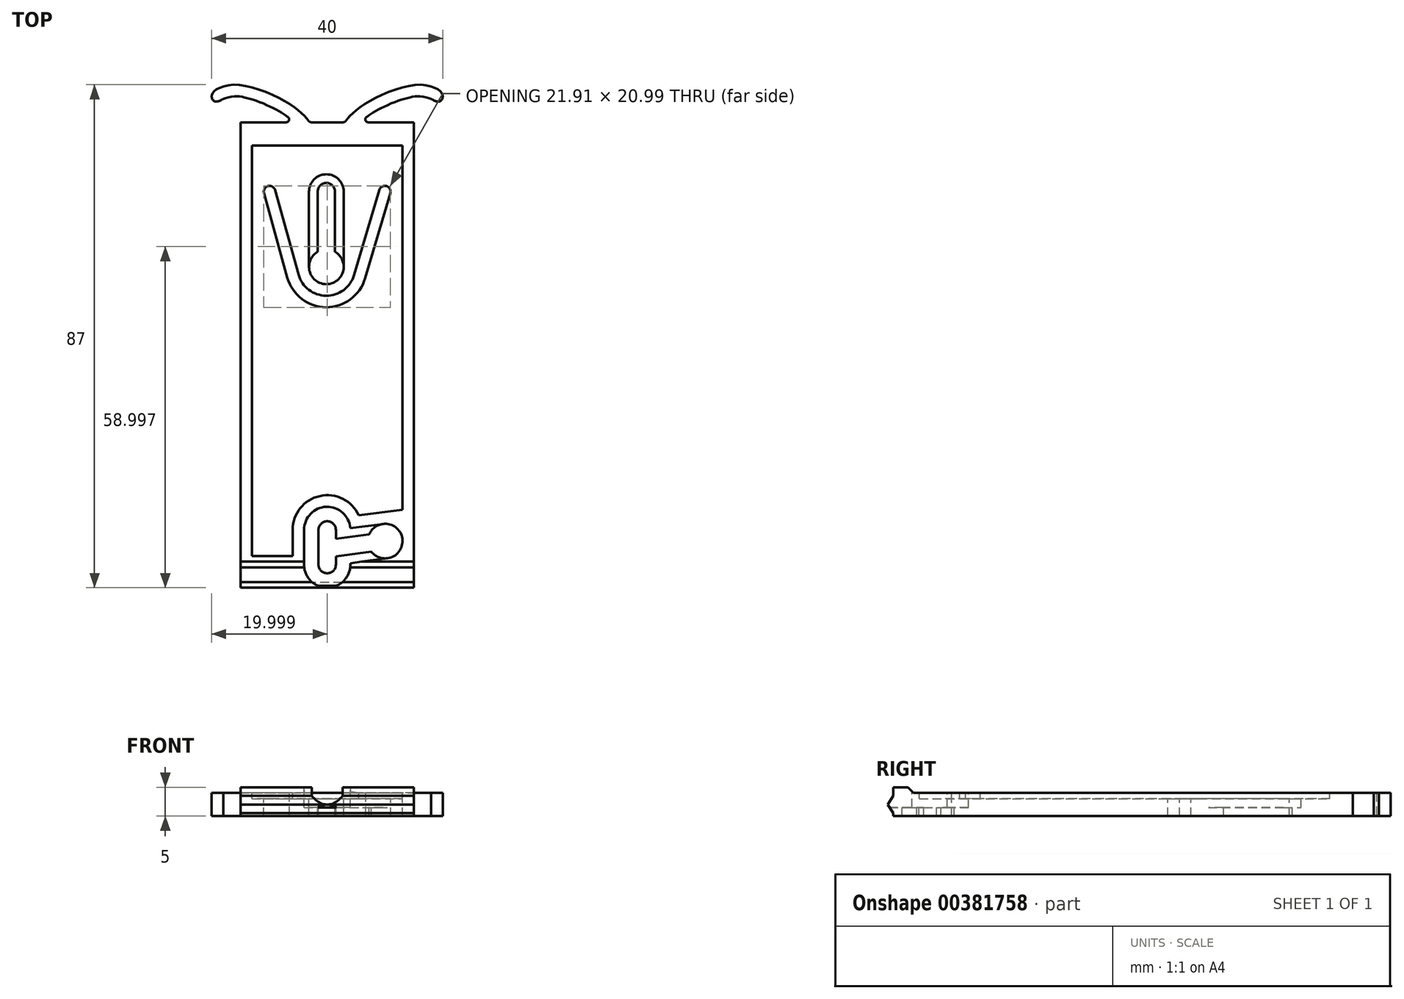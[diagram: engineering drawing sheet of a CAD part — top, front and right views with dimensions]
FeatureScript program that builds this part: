
annotation { "Feature Type Name" : "Feature", "Feature Type Description" : "" }
export const myFeature = defineFeature(function(context is Context, id is Id, definition is map)
    precondition{}
    {
        {
            var Q0;
            Q0=qCreatedBy(makeId("Top.planeOp"),FACE);
            var sketch = newSketch(context, id + "F0", { "sketchPlane" : qUnion([Q0])});
            skLineSegment(sketch, "E0.right", {"start": v(30.36, 0) * mm, "end": v(30.36, -80.5) * mm});
            skLineSegment(sketch, "E1", {"start": v(15.36, -84.44) * mm, "end": v(15.36, 27.39) * mm, "construction": true});
            skPoint(sketch, "E1.endSnap0", {"position": v(15.36, 0) * mm});
            skLineSegment(sketch, "E2", {"start": v(-4.64, 6.5) * mm, "end": v(31.36, 6.5) * mm, "construction": true});
            skLineSegment(sketch, "E3.MirrorCS", {"start": v(18.36, 6.5) * mm, "end": v(18.36, 0) * mm, "construction": true});
            skLineSegment(sketch, "E4.0", {"start": v(-5, 5.5) * mm, "end": v(35.36, 5.5) * mm, "construction": true});
            skLineSegment(sketch, "E5", {"start": v(31.36, 9.18) * mm, "end": v(31.36, -0.18) * mm, "construction": true});
            skLineSegment(sketch, "E6", {"start": v(14.49, 3) * mm, "end": v(22.26, 3) * mm, "construction": true});
            skLineSegment(sketch, "E7", {"start": v(21.36, 4) * mm, "end": v(21.36, 1.65) * mm, "construction": true});
            skLineSegment(sketch, "E8.trimOffspring", {"start": v(22.44, 0) * mm, "end": v(30.36, 0) * mm});
            skPoint(sketch, "E9.visualSharp", {"position": v(18.36, 0) * mm});
            skLineSegment(sketch, "E10", {"start": v(35.36, 5.5) * mm, "end": v(35.36, 4.5) * mm});
            skLineSegment(sketch, "E11.trimOffspring", {"start": v(31.82, 6.5) * mm, "end": v(35.36, 6.5) * mm, "construction": true});
            skFitSpline(sketch, "E12", {"points": [v(35.36, 4.5) * mm, v(35.09, 5.18) * mm, v(31.36, 6.5) * mm, v(21.36, 2.82) * mm, v(18.36, 0) * mm], "startDerivative": vector(-1.02, 6.23) * mm, "endDerivative": vector(-8.9, -10.77) * mm});
            skFitSpline(sketch, "E13.0", {"points": [v(34.37, 4.34) * mm, v(34.36, 4.4) * mm, v(34.35, 4.5) * mm, v(34.34, 4.51) * mm, v(34.34, 4.52) * mm, v(34.31, 4.55) * mm, v(34.25, 4.62) * mm, v(34.1, 4.74) * mm, v(33.84, 4.91) * mm, v(33.5, 5.09) * mm, v(32.95, 5.3) * mm, v(32.27, 5.45) * mm, v(31.49, 5.5) * mm, v(30.63, 5.48) * mm, v(29.4, 5.3) * mm, v(27.26, 4.7) * mm, v(24.5, 3.55) * mm, v(21.73, 1.95) * mm, v(20.2, 0.64) * mm, v(19.5, -0.19) * mm, v(19.13, -0.64) * mm], "construction": true});
            skPoint(sketch, "E14.third.point", {"position": v(33.58, 3.88) * mm});
            skPoint(sketch, "E15", {"position": v(31.36, 4.5) * mm});
            skPoint(sketch, "E16", {"position": v(27.51, 3.67) * mm});
            skPoint(sketch, "E17", {"position": v(24.47, 2.34) * mm});
            skPoint(sketch, "E18", {"position": v(21.04, 0) * mm});
            skPoint(sketch, "E19", {"position": v(22.66, 1.29) * mm});
            skPoint(sketch, "E20", {"position": v(29.8, 4.32) * mm});
            skFitSpline(sketch, "E21", {"points": [v(33.58, 3.88) * mm, v(33.32, 4.05) * mm, v(31.36, 4.5) * mm, v(29.8, 4.32) * mm, v(27.51, 3.67) * mm, v(24.47, 2.34) * mm, v(22.66, 1.29) * mm, v(21.04, 0) * mm], "startDerivative": vector(-2.9, 2.85) * mm, "endDerivative": vector(-10.67, -8.94) * mm});
            skPoint(sketch, "E22", {"position": v(33.84, 3.77) * mm});
            skPoint(sketch, "E23", {"position": v(34.3, 3.61) * mm});
            skPoint(sketch, "E24", {"position": v(34.8, 3.6) * mm});
            skPoint(sketch, "E25", {"position": v(35.23, 4) * mm});
            skFitSpline(sketch, "E26", {"points": [v(33.32, 4.05) * mm, v(33.84, 3.77) * mm, v(34.3, 3.61) * mm, v(34.8, 3.6) * mm, v(35.23, 4) * mm, v(35.36, 4.5) * mm], "startDerivative": vector(2.5, -1.5) * mm, "endDerivative": vector(0.35, 2.57) * mm});
            skLineSegment(sketch, "E27", {"start": v(18.13, 0) * mm, "end": v(15.36, 0) * mm});
            skLineSegment(sketch, "E28", {"start": v(30.36, -80.5) * mm, "end": v(15.36, -80.5) * mm});
            skArc(sketch, "E29.filletArc", {"start": v(18.13, 0) * mm, "mid": v(18.34, 0.05) * mm, "end": v(18.51, 0.18) * mm});
            skArc(sketch, "E30.filletArc", {"start": v(22.14, 0.9) * mm, "mid": v(21.97, 0.34) * mm, "end": v(22.44, 0) * mm});
            skLineSegment(sketch, "E31.MirrorCS", {"start": v(0.36, 0) * mm, "end": v(0.36, -80.5) * mm});
            skFitSpline(sketch, "E32.MirrorCS", {"points": [v(-2.86, 3.88) * mm, v(-2.6, 4.05) * mm, v(-0.64, 4.5) * mm, v(0.92, 4.32) * mm, v(3.21, 3.67) * mm, v(6.25, 2.34) * mm, v(8.06, 1.29) * mm, v(9.68, 0) * mm], "startDerivative": vector(2.9, 2.85) * mm, "endDerivative": vector(10.67, -8.94) * mm});
            skFitSpline(sketch, "E33.MirrorCS", {"points": [v(-2.86, 3.88) * mm, v(-2.6, 4.05) * mm, v(-0.64, 4.5) * mm, v(0.92, 4.32) * mm, v(3.21, 3.67) * mm, v(6.25, 2.34) * mm, v(8.06, 1.29) * mm, v(9.68, 0) * mm], "startDerivative": vector(2.9, 2.85) * mm, "endDerivative": vector(10.67, -8.94) * mm});
            skArc(sketch, "E34.MirrorCS", {"start": v(8.59, 0.9) * mm, "mid": v(8.75, 0.34) * mm, "end": v(8.28, 0) * mm});
            skLineSegment(sketch, "E35.MirrorCS", {"start": v(8.28, 0) * mm, "end": v(0.36, 0) * mm});
            skLineSegment(sketch, "E36.MirrorCS", {"start": v(12.6, 0) * mm, "end": v(15.36, 0) * mm});
            skFitSpline(sketch, "E37.MirrorCS", {"points": [v(-4.64, 4.5) * mm, v(-4.37, 5.18) * mm, v(-0.64, 6.5) * mm, v(9.36, 2.82) * mm, v(12.36, 0) * mm], "startDerivative": vector(1.02, 6.23) * mm, "endDerivative": vector(8.9, -10.77) * mm});
            skArc(sketch, "E38.MirrorCS", {"start": v(12.6, 0) * mm, "mid": v(12.38, 0.05) * mm, "end": v(12.21, 0.18) * mm});
            skFitSpline(sketch, "E39.MirrorCS", {"points": [v(-2.6, 4.05) * mm, v(-3.12, 3.77) * mm, v(-3.57, 3.61) * mm, v(-4.08, 3.6) * mm, v(-4.5, 4) * mm, v(-4.64, 4.5) * mm], "startDerivative": vector(-2.5, -1.5) * mm, "endDerivative": vector(-0.35, 2.57) * mm});
            skLineSegment(sketch, "E40.MirrorCS", {"start": v(0.36, -80.5) * mm, "end": v(15.36, -80.5) * mm});
            skSolve(sketch);
        }
        {
            var Q0;
            Q0 = qSketchRegion(id + "F0", true);
            extrude(context, id + "F1", {"entities" : qUnion([Q0]), "depth" : 6.5 * mm});
        }
        {
            var Q0;
            Q0=makeQuery(id+"F1.opExtrude","SWEPT_FACE",FACE,{"disambiguationData":[OSD([sQuery(id+"F0.wireOp",EDGE,"E31.MirrorCS")])]});
            var sketch = newSketch(context, id + "F2", { "sketchPlane" : qUnion([Q0])});
            skLineSegment(sketch, "E41", {"start": v(2, 1.5) * mm, "end": v(2, 0) * mm});
            skLineSegment(sketch, "E42", {"start": v(2, 0) * mm, "end": v(4, 0) * mm});
            skLineSegment(sketch, "E43", {"start": v(4, 0) * mm, "end": v(4, 1.5) * mm});
            skLineSegment(sketch, "E44", {"start": v(79.5, 0) * mm, "end": v(77.5, 0) * mm});
            skLineSegment(sketch, "E45", {"start": v(77.5, 0) * mm, "end": v(77.5, 1.5) * mm});
            skLineSegment(sketch, "E46.trimOffspring", {"start": v(77.5, 1.5) * mm, "end": v(4, 1.5) * mm});
            skLineSegment(sketch, "E47.trimOffspring", {"start": v(2, 1.5) * mm, "end": v(-6.65, 1.5) * mm});
            skLineSegment(sketch, "E48", {"start": v(80.5, 2) * mm, "end": v(80.5, 3.5) * mm, "construction": true});
            skLineSegment(sketch, "E49", {"start": v(79.5, 2) * mm, "end": v(80.5, 3.5) * mm});
            skLineSegment(sketch, "E50", {"start": v(80.5, 3.5) * mm, "end": v(80.5, 5) * mm, "construction": true});
            skLineSegment(sketch, "E51", {"start": v(80.5, 5) * mm, "end": v(79.5, 5) * mm, "construction": true});
            skLineSegment(sketch, "E52", {"start": v(79.5, 5) * mm, "end": v(80.5, 3.5) * mm});
            skLineSegment(sketch, "E53", {"start": v(79.5, 5) * mm, "end": v(79.5, 6.5) * mm});
            skLineSegment(sketch, "E54", {"start": v(79.5, 2) * mm, "end": v(79.5, 0) * mm});
            skLineSegment(sketch, "E55", {"start": v(79.5, 6.5) * mm, "end": v(77, 6.5) * mm});
            skLineSegment(sketch, "E56", {"start": v(77, 6.5) * mm, "end": v(77, 5.5) * mm, "construction": true});
            skLineSegment(sketch, "E57", {"start": v(77, 5.5) * mm, "end": v(76, 5.5) * mm, "construction": true});
            skLineSegment(sketch, "E58", {"start": v(77, 6.5) * mm, "end": v(76, 5.5) * mm});
            skLineSegment(sketch, "E59", {"start": v(76, 5.5) * mm, "end": v(-6.6, 5.5) * mm});
            skLineSegment(sketch, "E60", {"start": v(-6.65, 1.5) * mm, "end": v(-6.65, 0) * mm});
            skLineSegment(sketch, "E61", {"start": v(-6.65, 0) * mm, "end": v(0, 0) * mm});
            skLineSegment(sketch, "E62", {"start": v(0, 0) * mm, "end": v(0, 1.5) * mm});
            skLineSegment(sketch, "E63", {"start": v(-6.6, 5.5) * mm, "end": v(-6.6, 6.83) * mm});
            skLineSegment(sketch, "E64", {"start": v(-6.6, 6.83) * mm, "end": v(0, 6.83) * mm});
            skLineSegment(sketch, "E65", {"start": v(0, 6.83) * mm, "end": v(0, 5.5) * mm});
            skSolve(sketch);
        }
        {
            var Q0;
            {var subQ0=sQuery(id+"F2.wireOp",EDGE,"E58");Q0=makeQuery(id+"F2.imprint","IMPRINT",FACE,{"disambiguationData":[TD([[makeQuery(id+"F2.imprint","IMPRINT",EDGE,{"derivedFrom":subQ0}),-1.0]])]});}
            var Q1;
            {var subQ0=sQuery(id+"F2.wireOp",EDGE,"E43");Q1=makeQuery(id+"F2.imprint","IMPRINT",FACE,{"disambiguationData":[TD([[makeQuery(id+"F2.imprint","IMPRINT",EDGE,{"derivedFrom":subQ0}),-1.0]])]});}
            var Q2;
            {var subQ0=sQuery(id+"F2.wireOp",EDGE,"E41");Q2=makeQuery(id+"F2.imprint","IMPRINT",FACE,{"disambiguationData":[TD([[makeQuery(id+"F2.imprint","IMPRINT",EDGE,{"derivedFrom":subQ0}),-1.0]])]});}
            var Q3;
            {var subQ0=sQuery(id+"F2.wireOp",EDGE,"E52");Q3=makeQuery(id+"F2.imprint","IMPRINT",FACE,{"disambiguationData":[TD([[makeQuery(id+"F2.imprint","IMPRINT",EDGE,{"derivedFrom":subQ0}),1.0]])]});}
            var Q4;
            {var subQ0=sQuery(id+"F2.wireOp",EDGE,"E49");Q4=makeQuery(id+"F2.imprint","IMPRINT",FACE,{"disambiguationData":[TD([[makeQuery(id+"F2.imprint","IMPRINT",EDGE,{"derivedFrom":subQ0}),-1.0]])]});}
            var Q5;
            {var subQ4=sQuery(id+"F2.wireOp",EDGE,"E63");Q5=makeQuery(id+"F2.imprint","IMPRINT",FACE,{"disambiguationData":[TD([[makeQuery(id+"F2.imprint","IMPRINT",EDGE,{"derivedFrom":subQ4}),-1.0]])]});}
            var Q6;
            {var subQ0=sQuery(id+"F2.wireOp",EDGE,"E60");Q6=makeQuery(id+"F2.imprint","IMPRINT",FACE,{"disambiguationData":[TD([[makeQuery(id+"F2.imprint","IMPRINT",EDGE,{"derivedFrom":subQ0}),1.0]])]});}
            var Q7;
            Q7=sQuery(id+"F2.wireOp",EDGE,"E56");
            var Q8;
            Q8=sQuery(id+"F2.wireOp",EDGE,"E57");
            extrude(context, id + "F3", {"entities" : qUnion([Q0, Q1, Q2, Q3, Q4, Q5, Q6]), "operationType" : NewBodyOperationType.REMOVE, "surfaceEntities" : qUnion([Q7, Q8]), "endBound" : BoundingType.SYMMETRIC, "oppositeDirection" : true, "depth" : 100 * mm});
        }
        {
            var Q0;
            Q0=makeQuery(id+"F3.boolean.opBoolean","COPY",FACE,{"derivedFrom":makeQuery(id+"F3.opExtrude","SWEPT_FACE",FACE,{"disambiguationData":[OSD([sQuery(id+"F2.wireOp",EDGE,"E59")])]})});
            var sketch = newSketch(context, id + "F4", { "sketchPlane" : qUnion([Q0])});
            skLineSegment(sketch, "E66", {"start": v(2.36, -4) * mm, "end": v(28.36, -4) * mm});
            skLineSegment(sketch, "E67", {"start": v(28.36, -4) * mm, "end": v(28.36, -67) * mm});
            skLineSegment(sketch, "E68", {"start": v(2.36, -75) * mm, "end": v(2.36, -4) * mm});
            skLineSegment(sketch, "E69", {"start": v(9.36, -75) * mm, "end": v(9.36, -70.5) * mm});
            skLineSegment(sketch, "E70", {"start": v(15.36, -75) * mm, "end": v(15.36, -4) * mm, "construction": true});
            skPoint(sketch, "E71", {"position": v(15.36, -70.5) * mm});
            skArc(sketch, "E72.trimOffspring", {"start": v(20.82, -68) * mm, "mid": v(14.08, -64.64) * mm, "end": v(9.36, -70.5) * mm});
            skLineSegment(sketch, "E73.trimOffspring", {"start": v(9.36, -75) * mm, "end": v(2.36, -75) * mm});
            skPoint(sketch, "E74", {"position": v(20.82, -68) * mm});
            skLineSegment(sketch, "E75", {"start": v(28.36, -67) * mm, "end": v(20.82, -68) * mm});
            skPoint(sketch, "E76.orphan", {"position": v(21.36, -70.5) * mm});
            skSolve(sketch);
        }
        {
            var Q0;
            Q0 = qSketchRegion(id + "F4", true);
            extrude(context, id + "F5", {"entities" : qUnion([Q0]), "operationType" : NewBodyOperationType.REMOVE, "oppositeDirection" : true, "depth" : 1 * mm});
        }
        {
            var Q0;
            Q0=makeQuery(id+"F5.boolean.opBoolean","COPY",FACE,{"derivedFrom":makeQuery(id+"F5.opExtrude","CAP_FACE",FACE,{"disambiguationData":[OSD([sQuery(id+"F4.wireOp",EDGE,"E66"),sQuery(id+"F4.wireOp",EDGE,"E67"),sQuery(id+"F4.wireOp",EDGE,"E68"),sQuery(id+"F4.wireOp",EDGE,"E69"),sQuery(id+"F4.wireOp",EDGE,"3gRxLVl1-admC-iOb5-uZqX-NsdRVtH0Ynl3"),sQuery(id+"F4.wireOp",EDGE,"E72.trimOffspring"),sQuery(id+"F4.wireOp",EDGE,"E73.trimOffspring")])],"isStart":false})});
            var sketch = newSketch(context, id + "F6", { "sketchPlane" : qUnion([Q0])});
            skLineSegment(sketch, "E77", {"start": v(15.36, -4) * mm, "end": v(14.08, -74.45) * mm});
            skPoint(sketch, "E77.endSnap0", {"position": v(14.08, -64.64) * mm});
            skArc(sketch, "E78", {"start": v(18.22, -12) * mm, "mid": v(15.22, -9) * mm, "end": v(12.22, -12) * mm});
            skLineSegment(sketch, "E79", {"start": v(12.22, -12) * mm, "end": v(18.22, -12) * mm, "construction": true});
            skLineSegment(sketch, "E80", {"start": v(18.22, -12) * mm, "end": v(18.22, -25) * mm});
            skLineSegment(sketch, "E81", {"start": v(18.22, -25) * mm, "end": v(12.22, -25) * mm, "construction": true});
            skLineSegment(sketch, "E82", {"start": v(12.22, -25) * mm, "end": v(12.22, -12) * mm});
            skArc(sketch, "E83", {"start": v(12.22, -25) * mm, "mid": v(15.22, -28) * mm, "end": v(18.22, -25) * mm});
            skSolve(sketch);
        }
        {
            var Q0;
            Q0 = qSketchRegion(id + "F6", true);
            extrude(context, id + "F7", {"entities" : qUnion([Q0]), "operationType" : NewBodyOperationType.REMOVE, "oppositeDirection" : true, "depth" : 1.5 * mm});
        }
        {
            var Q0;
            Q0=makeQuery(id+"F7.boolean.opBoolean","COPY",FACE,{"derivedFrom":makeQuery(id+"F7.opExtrude","CAP_FACE",FACE,{"disambiguationData":[OSD([sQuery(id+"F6.wireOp",EDGE,"E78"),sQuery(id+"F6.wireOp",EDGE,"E80"),sQuery(id+"F6.wireOp",EDGE,"E82"),sQuery(id+"F6.wireOp",EDGE,"E83")])],"isStart":false})});
            var sketch = newSketch(context, id + "F8", { "sketchPlane" : qUnion([Q0])});
            skLineSegment(sketch, "E84", {"start": v(15.22, -9) * mm, "end": v(15.22, -28) * mm, "construction": true});
            skArc(sketch, "E85", {"start": v(13.72, -22.4) * mm, "mid": v(15.22, -28) * mm, "end": v(16.72, -22.4) * mm});
            skArc(sketch, "E86", {"start": v(16.72, -12) * mm, "mid": v(15.22, -10.5) * mm, "end": v(13.72, -12) * mm});
            skLineSegment(sketch, "E87", {"start": v(16.72, -12) * mm, "end": v(16.72, -22.4) * mm});
            skLineSegment(sketch, "E88", {"start": v(13.72, -12) * mm, "end": v(13.72, -22.4) * mm});
            skSolve(sketch);
        }
        {
            var Q0;
            Q0 = qSketchRegion(id + "F8", true);
            extrude(context, id + "F9", {"entities" : qUnion([Q0]), "operationType" : NewBodyOperationType.REMOVE, "endBound" : BoundingType.THROUGH_ALL, "oppositeDirection" : true, "depth" : 25 * mm});
        }
        {
            var Q0;
            Q0=makeQuery(id+"F1.opExtrude","CAP_FACE",FACE,{"disambiguationData":[OSD([sQuery(id+"F0.wireOp",EDGE,"E0.right"),sQuery(id+"F0.wireOp",EDGE,"E8.trimOffspring"),sQuery(id+"F0.wireOp",EDGE,"E12"),sQuery(id+"F0.wireOp",EDGE,"E21"),sQuery(id+"F0.wireOp",EDGE,"E26"),sQuery(id+"F0.wireOp",EDGE,"E27"),sQuery(id+"F0.wireOp",EDGE,"E28"),sQuery(id+"F0.wireOp",EDGE,"E29.filletArc"),sQuery(id+"F0.wireOp",EDGE,"E30.filletArc"),sQuery(id+"F0.wireOp",EDGE,"E31.MirrorCS"),sQuery(id+"F0.wireOp",EDGE,"E32.MirrorCS"),sQuery(id+"F0.wireOp",EDGE,"E34.MirrorCS"),sQuery(id+"F0.wireOp",EDGE,"E35.MirrorCS"),sQuery(id+"F0.wireOp",EDGE,"E36.MirrorCS"),sQuery(id+"F0.wireOp",EDGE,"E37.MirrorCS"),sQuery(id+"F0.wireOp",EDGE,"E38.MirrorCS"),sQuery(id+"F0.wireOp",EDGE,"E39.MirrorCS"),sQuery(id+"F0.wireOp",EDGE,"E40.MirrorCS")])],"isStart":false});
            var sketch = newSketch(context, id + "F10", { "sketchPlane" : qUnion([Q0])});
            skArc(sketch, "E89.0", {"start": v(19.35, -70.21) * mm, "mid": v(15.22, -66.5) * mm, "end": v(11.36, -70.5) * mm});
            skLineSegment(sketch, "E89.1", {"start": v(11.36, -76.5) * mm, "end": v(11.36, -70.5) * mm});
            skLineSegment(sketch, "E90.0", {"start": v(19.35, -76.26) * mm, "end": v(25.78, -75.41) * mm});
            skLineSegment(sketch, "E91", {"start": v(11.36, -73.5) * mm, "end": v(14.22, -73.5) * mm, "construction": true});
            skArc(sketch, "E92.MirrorCS", {"start": v(19.35, -76.26) * mm, "mid": v(15.48, -80.5) * mm, "end": v(11.36, -76.5) * mm});
            skLineSegment(sketch, "E93.0", {"start": v(19.35, -73.24) * mm, "end": v(29.53, -71.89) * mm, "construction": true});
            skPoint(sketch, "E94", {"position": v(25.39, -72.44) * mm});
            skPoint(sketch, "E95", {"position": v(28.36, -72.04) * mm});
            skArc(sketch, "E96", {"start": v(25.78, -75.41) * mm, "mid": v(28.36, -72.04) * mm, "end": v(25, -69.46) * mm});
            skPoint(sketch, "E97.orphan", {"position": v(19.36, -70.5) * mm});
            skPoint(sketch, "E98.orphan", {"position": v(19.36, -76.5) * mm});
            skLineSegment(sketch, "E99", {"start": v(19.35, -70.21) * mm, "end": v(25, -69.46) * mm});
            skSolve(sketch);
        }
        {
            var Q0;
            Q0 = qSketchRegion(id + "F10", true);
            extrude(context, id + "F11", {"entities" : qUnion([Q0]), "operationType" : NewBodyOperationType.REMOVE, "oppositeDirection" : true, "depth" : 3.5 * mm});
        }
        {
            var Q0;
            Q0=makeQuery(id+"F11.boolean.opBoolean","COPY",FACE,{"derivedFrom":makeQuery(id+"F11.opExtrude","CAP_FACE",FACE,{"disambiguationData":[OSD([sQuery(id+"F10.wireOp",EDGE,"E89.0"),sQuery(id+"F10.wireOp",EDGE,"E89.1"),sQuery(id+"F10.wireOp",EDGE,"c576aeb2-b4bf-4eb0-8949-e53386425e69.0"),sQuery(id+"F10.wireOp",EDGE,"E90.0"),sQuery(id+"F10.wireOp",EDGE,"E92.MirrorCS"),sQuery(id+"F10.wireOp",EDGE,"E96")])],"isStart":false})});
            var sketch = newSketch(context, id + "F12", { "sketchPlane" : qUnion([Q0])});
            skLineSegment(sketch, "E100", {"start": v(15.36, -70.5) * mm, "end": v(15.36, -76.5) * mm});
            skCircle(sketch, "E101", {"center": v(15.36, -70.5) * mm, "radius": 1.5 * mm});
            skArc(sketch, "E102", {"start": v(15.36, -75) * mm, "mid": v(14.3, -77.56) * mm, "end": v(16.86, -76.5) * mm});
            skLineSegment(sketch, "E103", {"start": v(13.86, -70.5) * mm, "end": v(13.86, -76.5) * mm});
            skLineSegment(sketch, "E104", {"start": v(13.86, -76.5) * mm, "end": v(16.86, -76.5) * mm});
            skLineSegment(sketch, "E105", {"start": v(16.86, -76.5) * mm, "end": v(16.86, -75.08) * mm});
            skLineSegment(sketch, "E106", {"start": v(16.86, -70.5) * mm, "end": v(13.86, -70.5) * mm});
            skLineSegment(sketch, "E107.trimOffspring", {"start": v(16.86, -72.05) * mm, "end": v(16.86, -70.5) * mm});
            skLineSegment(sketch, "E108.0", {"start": v(16.86, -72.05) * mm, "end": v(22.61, -71.3) * mm});
            skPoint(sketch, "E109", {"position": v(25.39, -72.44) * mm});
            skCircle(sketch, "E110", {"center": v(25.39, -72.44) * mm, "radius": 3 * mm});
            skLineSegment(sketch, "E111.0", {"start": v(16.86, -75.08) * mm, "end": v(23, -74.27) * mm});
            skSolve(sketch);
        }
        {
            var Q0;
            {var subQ0=sQuery(id+"F12.wireOp",EDGE,"E106");var subQ1=sQuery(id+"F12.wireOp",EDGE,"E100");var subQ2=makeQuery(id+"F12.imprint","INTERSECT",VERTEX,{"derivedFrom":[subQ1,subQ0]});Q0=makeQuery(id+"F12.imprint","IMPRINT",FACE,{"disambiguationData":[TD([[makeQuery(id+"F12.imprint","IMPRINT",EDGE,{"disambiguationData":[TD([[subQ2,-1.0]])],"derivedFrom":subQ1}),-1.0]])]});}
            var Q1;
            {var subQ0=sQuery(id+"F12.wireOp",EDGE,"E104");var subQ1=sQuery(id+"F12.wireOp",EDGE,"E100");var subQ2=makeQuery(id+"F12.imprint","INTERSECT",VERTEX,{"derivedFrom":[subQ1,subQ0]});Q1=makeQuery(id+"F12.imprint","IMPRINT",FACE,{"disambiguationData":[TD([[makeQuery(id+"F12.imprint","IMPRINT",EDGE,{"disambiguationData":[TD([[subQ2,1.0]])],"derivedFrom":subQ1}),-1.0]])]});}
            var Q2;
            {var subQ0=sQuery(id+"F12.wireOp",EDGE,"E106");var subQ4=makeQuery(id+"F12.imprint","INTERSECT",VERTEX,{"derivedFrom":[sQuery(id+"F12.wireOp",EDGE,"E100"),subQ0]});Q2=makeQuery(id+"F12.imprint","IMPRINT",FACE,{"disambiguationData":[TD([[makeQuery(id+"F12.imprint","IMPRINT",EDGE,{"disambiguationData":[TD([[subQ4,1.0]])],"derivedFrom":subQ0}),-1.0]])]});}
            var Q3;
            {var subQ0=sQuery(id+"F12.wireOp",EDGE,"E104");var subQ4=makeQuery(id+"F12.imprint","INTERSECT",VERTEX,{"derivedFrom":[sQuery(id+"F12.wireOp",EDGE,"E100"),subQ0]});Q3=makeQuery(id+"F12.imprint","IMPRINT",FACE,{"disambiguationData":[TD([[makeQuery(id+"F12.imprint","IMPRINT",EDGE,{"disambiguationData":[TD([[subQ4,1.0]])],"derivedFrom":subQ0}),-1.0]])]});}
            var Q4;
            {var subQ5=sQuery(id+"F12.wireOp",EDGE,"E103");Q4=makeQuery(id+"F12.imprint","IMPRINT",FACE,{"disambiguationData":[TD([[makeQuery(id+"F12.imprint","IMPRINT",EDGE,{"derivedFrom":subQ5}),1.0]])]});}
            var Q5;
            {var subQ0=sQuery(id+"F12.wireOp",EDGE,"E105");Q5=makeQuery(id+"F12.imprint","IMPRINT",FACE,{"disambiguationData":[TD([[makeQuery(id+"F12.imprint","IMPRINT",EDGE,{"derivedFrom":subQ0}),1.0]])]});}
            var Q6;
            {var subQ0=sQuery(id+"F12.wireOp",EDGE,"E106");var subQ1=sQuery(id+"F12.wireOp",EDGE,"E100");var subQ2=makeQuery(id+"F12.imprint","INTERSECT",VERTEX,{"derivedFrom":[subQ1,subQ0]});Q6=makeQuery(id+"F12.imprint","IMPRINT",FACE,{"disambiguationData":[TD([[makeQuery(id+"F12.imprint","IMPRINT",EDGE,{"disambiguationData":[TD([[subQ2,-1.0]])],"derivedFrom":subQ1}),1.0]])]});}
            var Q7;
            {var subQ0=sQuery(id+"F12.wireOp",EDGE,"E110");var subQ1=makeQuery(id+"F12.imprint","INTERSECT",VERTEX,{"derivedFrom":[makeQuery(id+"F11.boolean.opBoolean","COPY",EDGE,{"derivedFrom":makeQuery(id+"F11.opExtrude","CAP_EDGE",EDGE,{"disambiguationData":[OSD([sQuery(id+"F10.wireOp",EDGE,"E90.0")])],"isStart":false})}),subQ0]});Q7=makeQuery(id+"F12.imprint","IMPRINT",FACE,{"disambiguationData":[TD([[makeQuery(id+"F12.imprint","IMPRINT",EDGE,{"disambiguationData":[TD([[subQ1,-1.0]])],"derivedFrom":subQ0}),1.0]])]});}
            extrude(context, id + "F13", {"entities" : qUnion([Q0, Q1, Q2, Q3, Q4, Q5, Q6, Q7]), "operationType" : NewBodyOperationType.REMOVE, "endBound" : BoundingType.THROUGH_ALL, "oppositeDirection" : true, "depth" : 25 * mm});
        }
        {
            var Q0;
            Q0=makeQuery(id+"F5.boolean.opBoolean","COPY",FACE,{"derivedFrom":makeQuery(id+"F5.opExtrude","CAP_FACE",FACE,{"disambiguationData":[OSD([sQuery(id+"F4.wireOp",EDGE,"E66"),sQuery(id+"F4.wireOp",EDGE,"E67"),sQuery(id+"F4.wireOp",EDGE,"E68"),sQuery(id+"F4.wireOp",EDGE,"E69"),sQuery(id+"F4.wireOp",EDGE,"E72.trimOffspring"),sQuery(id+"F4.wireOp",EDGE,"E73.trimOffspring"),sQuery(id+"F4.wireOp",EDGE,"E75")])],"isStart":false})});
            var sketch = newSketch(context, id + "F14", { "sketchPlane" : qUnion([Q0])});
            skArc(sketch, "E112.0", {"start": v(10.4, -26.33) * mm, "mid": v(15.17, -30) * mm, "end": v(20.01, -26.42) * mm});
            skArc(sketch, "E113.0", {"start": v(8.47, -26.86) * mm, "mid": v(15.15, -32) * mm, "end": v(21.93, -26.99) * mm});
            skLineSegment(sketch, "E114", {"start": v(5.4, -11) * mm, "end": v(25.32, -11) * mm, "construction": true});
            skLineSegment(sketch, "E115", {"start": v(2.36, -12) * mm, "end": v(28.36, -12) * mm, "construction": true});
            skPoint(sketch, "E116", {"position": v(4.36, -12) * mm});
            skPoint(sketch, "E117", {"position": v(26.36, -12) * mm});
            skLineSegment(sketch, "E118", {"start": v(26.28, -12.28) * mm, "end": v(21.93, -26.99) * mm});
            skLineSegment(sketch, "E119", {"start": v(4.43, -12.27) * mm, "end": v(8.47, -26.86) * mm});
            skLineSegment(sketch, "E120.0", {"start": v(6.36, -11.73) * mm, "end": v(10.4, -26.33) * mm});
            skLineSegment(sketch, "E121.0", {"start": v(24.36, -11.72) * mm, "end": v(20.01, -26.42) * mm});
            skArc(sketch, "E122.filletArc", {"start": v(5.4, -11) * mm, "mid": v(4.6, -11.4) * mm, "end": v(4.43, -12.27) * mm});
            skPoint(sketch, "E123.visualSharp", {"position": v(6.16, -11) * mm});
            skArc(sketch, "E123.filletArc", {"start": v(6.36, -11.73) * mm, "mid": v(6, -11.2) * mm, "end": v(5.4, -11) * mm});
            skArc(sketch, "E124.filletArc", {"start": v(26.28, -12.28) * mm, "mid": v(26.12, -11.4) * mm, "end": v(25.32, -11) * mm});
            skPoint(sketch, "E125.visualSharp", {"position": v(24.57, -11) * mm});
            skArc(sketch, "E125.filletArc", {"start": v(25.32, -11) * mm, "mid": v(24.72, -11.2) * mm, "end": v(24.36, -11.72) * mm});
            skSolve(sketch);
        }
        {
            var Q0;
            Q0 = qSketchRegion(id + "F14", true);
            extrude(context, id + "F15", {"entities" : qUnion([Q0]), "operationType" : NewBodyOperationType.REMOVE, "endBound" : BoundingType.THROUGH_ALL, "oppositeDirection" : true, "depth" : 25 * mm});
        }
        {
            var Q0;
            Q0=makeQuery(id+"F1.opExtrude","SWEPT_FACE",FACE,{"disambiguationData":[OSD([sQuery(id+"F0.wireOp",EDGE,"E0.right")])]});
            var sketch = newSketch(context, id + "F16", { "sketchPlane" : qUnion([Q0])});
            skLineSegment(sketch, "E126", {"start": v(-80.37, 1.5) * mm, "end": v(7.8, 1.5) * mm});
            skPoint(sketch, "E126.endSnap0", {"position": v(-1, 1.5) * mm});
            skLineSegment(sketch, "E127", {"start": v(7.8, 1.5) * mm, "end": v(7.8, -2.07) * mm});
            skLineSegment(sketch, "E128", {"start": v(7.8, -2.07) * mm, "end": v(-80.37, -2.07) * mm});
            skLineSegment(sketch, "E129", {"start": v(-80.37, -2.07) * mm, "end": v(-80.37, 1.5) * mm});
            skSolve(sketch);
        }
        {
            var Q0;
            {var subQ1=makeQuery(id+"F3.opExtrude","SWEPT_FACE",FACE,{"disambiguationData":[OSD([sQuery(id+"F2.wireOp",EDGE,"E45")])]});var subQ2=sQuery(id+"F0.wireOp",EDGE,"E0.right");var subQ3=makeQuery(id+"F1.opExtrude","SWEPT_FACE",FACE,{"disambiguationData":[OSD([subQ2])]});var subQ4=makeQuery(id+"F3.boolean.opBoolean","INTERSECT",EDGE,{"derivedFrom":[subQ3,subQ1]});Q0=makeQuery(id+"F16.imprint","IMPRINT",FACE,{"disambiguationData":[TD([[makeQuery(id+"F16.imprint","IMPRINT",EDGE,{"derivedFrom":subQ4}),-1.0]])]});}
            var Q1;
            {var subQ1=makeQuery(id+"F3.opExtrude","SWEPT_FACE",FACE,{"disambiguationData":[OSD([sQuery(id+"F2.wireOp",EDGE,"E41")])]});var subQ2=sQuery(id+"F0.wireOp",EDGE,"E0.right");var subQ3=makeQuery(id+"F1.opExtrude","SWEPT_FACE",FACE,{"disambiguationData":[OSD([subQ2])]});var subQ4=makeQuery(id+"F3.boolean.opBoolean","INTERSECT",EDGE,{"derivedFrom":[subQ3,subQ1]});Q1=makeQuery(id+"F16.imprint","IMPRINT",FACE,{"disambiguationData":[TD([[makeQuery(id+"F16.imprint","IMPRINT",EDGE,{"derivedFrom":subQ4}),1.0]])]});}
            extrude(context, id + "F17", {"entities" : qUnion([Q0, Q1]), "operationType" : NewBodyOperationType.REMOVE, "endBound" : BoundingType.THROUGH_ALL, "oppositeDirection" : true, "depth" : 25 * mm});
        }
    });
